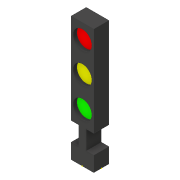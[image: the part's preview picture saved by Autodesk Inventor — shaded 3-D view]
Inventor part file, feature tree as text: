
AUTODESK INVENTOR PART (.ipt)
format: ipt  version: 2018 (Build 220112000, 112)  size: 145,408 bytes
history: native  units: in
note: dims shown in document units (in); Inventor stores cm internally (conversion verified against a paired STEP export)
features: sketch x10, extrude x6
ambient origin geometry x8: Origin, YZ Plane, XZ Plane, XY Plane, X Axis, Y Axis, Z Axis, Center Point
bodies: Solid1 (feature_tree)
feature tree (16):
  sketch  "Sketch1"  dims[d0=1.1811in d1=0.7874in]
  extrude  "Extrusion1"  Depth=0.7874in
  extrude  "Extrusion2"  Depth=0.5906in
  extrude  "Extrusion3"  Depth=0.3937in
  sketch  "Sketch5"  dims[d9=0.1969in d10=0.7874in d11=0.0in]
  extrude  "Extrusion4"  TaperAngle=0.0deg  [1 undecoded]
  extrude  "Extrusion5"  Depth=0.7874in TaperAngle=0.0deg
  extrude  "Extrusion6"  Depth=4.7244in
  sketch  "Sketch9"  dims[d16=0.7874in d17=0.0in]
  sketch  "Sketch10"  dims[d18=1.5748in d19=1.5748in d20=0.7874in d21=0.7874in d22=0.7874in d23=0.9843in d24=0.1969in d25=0.0in d26=2.3622in d27=0.9843in d28=0.1969in d29=0.0in d30=0.7874in d31=0.9843in d32=0.1969in d33=0.0in]
  sketch  "Sketch2"  dims[d2=0.7874in d3=0.5906in]
  sketch  "Sketch3"  dims[d4=0.7874in d5=0.0in d6=0.3937in]
  sketch  "Sketch4"  dims[d7=0.9843in d8=0.0in]
  sketch  "Sketch6"  dims[d12=1.1811in d13=4.7244in]
  sketch  "Sketch7"  dims[d14=0.0in]
  sketch  "Sketch8"  dims[d15=0.5906in]
note: 1 required parameter value undecoded (feature->parameter linkage not recoverable at this tier; creation-order binding heuristic only, values carry confidence <= 0.55)
